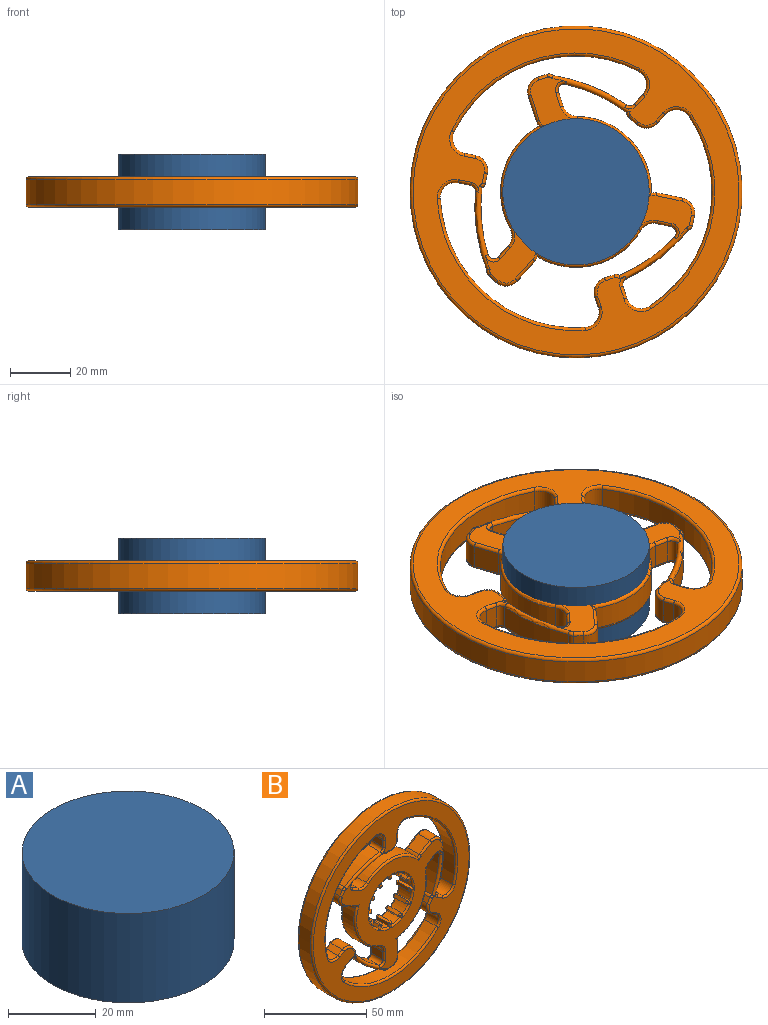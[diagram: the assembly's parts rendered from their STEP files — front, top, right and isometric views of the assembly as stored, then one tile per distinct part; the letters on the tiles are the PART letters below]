
ASSEMBLY  parts=2 mates=1
PART A: 3 faces, bbox 48.5x48.5x25 mm
  f0: cylinder r=24.24mm len=48.48mm, axis (0,0,-1), area 3807.4mm2, adj f1,f2
  f1: plane 48.48x48.48mm, normal (0,0,1), area 1845.8mm2, adj f0
  f2: plane 48.48x48.48mm, normal (0,0,-1), area 1845.8mm2, adj f0
PART B: 301 faces, bbox 119.1x10x119.1 mm
  f0: plane 108x108mm, normal (0,1,0), area 2938.6mm2, adj f185,f188,f189,f192,f193,f196,f197,f199
  f1: plane 108x108mm, normal (0,-1,0), area 2938.6mm2, adj f242,f245,f246,f249,f250,f253,f254,f256
  f2: cylinder r=15mm len=8mm, axis (0,1,0), area 46.8mm2, adj f109,f110,f148,f184
  f3: cylinder r=15mm len=8mm, axis (0,1,0), area 46.8mm2, adj f106,f107,f143,f179
  f4: cylinder r=15mm len=8mm, axis (0,1,0), area 46.8mm2, adj f103,f104,f137,f173
  f5: cylinder r=15mm len=8mm, axis (0,1,0), area 46.8mm2, adj f100,f101,f131,f167
  f6: cylinder r=15mm len=8mm, axis (0,1,0), area 46.8mm2, adj f97,f98,f125,f161
  f7: cylinder r=15mm len=8mm, axis (0,1,0), area 46.8mm2, adj f94,f95,f119,f155
  f8: cylinder r=15mm len=8mm, axis (0,1,0), area 46.8mm2, adj f91,f92,f113,f149
  f9: cylinder r=15mm len=8mm, axis (0,1,0), area 46.8mm2, adj f88,f89,f118,f154
  f10: cylinder r=15mm len=8mm, axis (0,1,0), area 46.8mm2, adj f85,f86,f124,f160
  f11: cylinder r=15mm len=8mm, axis (0,1,0), area 46.8mm2, adj f82,f83,f130,f166
  f12: cylinder r=15mm len=8mm, axis (0,1,0), area 46.8mm2, adj f79,f80,f136,f172
  f13: cylinder r=15mm len=8mm, axis (0,1,0), area 46.8mm2, adj f77,f112,f142,f178
  f14: plane 8x3.59mm, normal (0.5,0,-0.87), area 33.2mm2, adj f58,f65,f189,f249
  f15: plane 8x3.59mm, normal (0.5,0,0.87), area 33.2mm2, adj f61,f67,f210,f269
  f16: plane 8x4.15mm, normal (-1,0,0), area 33.2mm2, adj f64,f69,f230,f288
  f17: cylinder r=45mm len=55.61mm, axis (0,1,0), area 572.1mm2, adj f57,f64,f222,f280
  f18: cylinder r=45mm len=64.22mm, axis (0,1,0), area 572.1mm2, adj f58,f60,f188,f242
  f19: cylinder r=45mm len=55.61mm, axis (0,1,0), area 572.1mm2, adj f61,f63,f217,f277
  f20: cylinder r=55mm len=110mm, axis (0,1,0), area 2764.6mm2, adj f299,f300
  f21: plane 69.83x64.18mm, normal (0,-1,0), area 1385.1mm2, adj f113,f118,f119,f124,f125,f130,f131,f136
  f22: plane 69.83x64.18mm, normal (0,1,0), area 1385.1mm2, adj f149,f154,f155,f160,f161,f166,f167,f172
  f23: plane 8x3.42mm, normal (0,0,-1), area 27.4mm2, adj f62,f76,f233,f293
  f24: plane 8x3.73mm, normal (1,0,0), area 29.8mm2, adj f62,f63,f225,f285
  f25: plane 8x2.96mm, normal (-0.87,0,0.5), area 27.4mm2, adj f59,f75,f201,f257
  f26: plane 8x3.23mm, normal (-0.5,0,-0.87), area 29.8mm2, adj f59,f60,f196,f250
  f27: plane 8x2.96mm, normal (0.87,0,0.5), area 27.4mm2, adj f56,f74,f206,f265
  f28: plane 8x3.23mm, normal (-0.5,0,0.87), area 29.8mm2, adj f56,f57,f214,f272
  f29: cylinder r=55mm len=21.31mm, axis (0,1,0), area 179.4mm2, adj f70,f76,f238,f295
  f30: cylinder r=57mm len=24.52mm, axis (0,1,0), area 210.7mm2, adj f69,f72,f238,f295
  f31: cylinder r=25mm len=29.23mm, axis (0,1,0), area 313mm2, adj f47,f54,f195,f251
  f32: cylinder r=25mm len=35.17mm, axis (0,1,0), area 313mm2, adj f49,f50,f236,f290
  f33: cylinder r=25mm len=31.69mm, axis (0,1,0), area 313mm2, adj f52,f55,f215,f271
  f34: plane 8x4.89mm, normal (-1,0,0), area 39.1mm2, adj f55,f66,f207,f264
  f35: plane 8x3.22mm, normal (0,0,-1), area 25.8mm2, adj f53,f73,f190,f248
  f36: plane 8.73x8mm, normal (1,0,0), area 69.8mm2, adj f53,f54,f187,f243
  f37: plane 8x4.24mm, normal (0.5,0,0.87), area 39.1mm2, adj f50,f70,f240,f297
  f38: plane 8x2.79mm, normal (-0.87,0,0.5), area 25.8mm2, adj f51,f72,f231,f287
  f39: plane 8x7.56mm, normal (-0.5,0,-0.87), area 69.8mm2, adj f51,f52,f223,f279
  f40: plane 8x4.24mm, normal (0.5,0,-0.87), area 39.1mm2, adj f47,f68,f200,f258
  f41: plane 8x2.79mm, normal (0.87,0,0.5), area 25.8mm2, adj f48,f71,f220,f274
  f42: plane 8x7.56mm, normal (-0.5,0,0.87), area 69.8mm2, adj f48,f49,f228,f282
  f43: cylinder r=55mm len=21.7mm, axis (0,1,0), area 179.4mm2, adj f68,f75,f208,f263
  f44: cylinder r=57mm len=25.71mm, axis (0,1,0), area 210.7mm2, adj f67,f71,f208,f263
  f45: cylinder r=55mm len=16.27mm, axis (0,1,0), area 179.4mm2, adj f66,f74,f197,f256
  f46: cylinder r=57mm len=20.01mm, axis (0,1,0), area 210.7mm2, adj f65,f73,f197,f256
  f47: cylinder r=5mm len=8mm, axis (0,1,0), area 49.5mm2, adj f31,f40,f198,f255
  f48: cylinder r=5mm len=8mm, axis (0,-1,0), area 62.8mm2, adj f41,f42,f224,f278
  f49: cylinder r=5mm len=8mm, axis (0,1,0), area 14.3mm2, adj f32,f42,f232,f286
  f50: cylinder r=5mm len=8mm, axis (0,1,0), area 49.5mm2, adj f32,f37,f239,f294
  f51: cylinder r=5mm len=8mm, axis (0,-1,0), area 62.8mm2, adj f38,f39,f227,f283
  f52: cylinder r=5mm len=8mm, axis (0,1,0), area 14.3mm2, adj f33,f39,f219,f275
  f53: cylinder r=5mm len=8mm, axis (0,-1,0), area 62.8mm2, adj f35,f36,f186,f244
  f54: cylinder r=5mm len=8mm, axis (0,1,0), area 14.3mm2, adj f31,f36,f191,f247
  f55: cylinder r=5mm len=8mm, axis (0,1,0), area 49.5mm2, adj f33,f34,f212,f267
  f56: cylinder r=5mm len=8mm, axis (0,-1,0), area 62.8mm2, adj f27,f28,f211,f268
  f57: cylinder r=5mm len=8mm, axis (0,1,0), area 72.9mm2, adj f17,f28,f218,f276
  f58: cylinder r=5mm len=8mm, axis (0,1,0), area 72.9mm2, adj f14,f18,f185,f245
  f59: cylinder r=5mm len=8mm, axis (0,-1,0), area 62.8mm2, adj f25,f26,f199,f254
  f60: cylinder r=5mm len=8mm, axis (0,1,0), area 72.9mm2, adj f18,f26,f192,f246
  f61: cylinder r=5mm len=8mm, axis (0,1,0), area 72.9mm2, adj f15,f19,f213,f273
  f62: cylinder r=5mm len=8mm, axis (0,-1,0), area 62.8mm2, adj f23,f24,f229,f289
  f63: cylinder r=5mm len=8mm, axis (0,1,0), area 72.9mm2, adj f19,f24,f221,f281
  f64: cylinder r=5mm len=8mm, axis (0,1,0), area 72.9mm2, adj f16,f17,f226,f284
  f65: cylinder r=2mm len=8mm, axis (0,1,0), area 23.2mm2, adj f14,f46,f193,f253
  f66: cylinder r=2mm len=8mm, axis (0,1,0), area 33.9mm2, adj f34,f45,f203,f261
  f67: cylinder r=2mm len=8mm, axis (0,1,0), area 23.2mm2, adj f15,f44,f209,f266
  f68: cylinder r=2mm len=8mm, axis (0,1,0), area 33.9mm2, adj f40,f43,f204,f260
  f69: cylinder r=2mm len=8mm, axis (0,1,0), area 23.2mm2, adj f16,f30,f234,f292
  f70: cylinder r=2mm len=8mm, axis (0,1,0), area 33.9mm2, adj f29,f37,f241,f298
  f71: cylinder r=2mm len=8mm, axis (0,1,0), area 17.5mm2, adj f41,f44,f216,f270
  f72: cylinder r=2mm len=8mm, axis (0,1,0), area 17.5mm2, adj f30,f38,f235,f291
  f73: cylinder r=2mm len=8mm, axis (0,1,0), area 17.5mm2, adj f35,f46,f194,f252
  f74: cylinder r=2mm len=8mm, axis (0,1,0), area 14.6mm2, adj f27,f45,f202,f262
  f75: cylinder r=2mm len=8mm, axis (0,1,0), area 14.6mm2, adj f25,f43,f205,f259
  f76: cylinder r=2mm len=8mm, axis (0,1,0), area 14.6mm2, adj f23,f29,f237,f296
  f77: plane 8x1.97mm, normal (-1,0,0), area 15.8mm2, adj f13,f78,f138,f175
  f78: plane 8x2mm, normal (0,0,-1), area 16mm2, adj f77,f79,f139,f174
  f79: plane 8x1.96mm, normal (1,0,0), area 15.7mm2, adj f12,f78,f138,f175
  f80: plane 8x1.71mm, normal (-0.87,0,0.5), area 15.8mm2, adj f12,f81,f132,f169
  f81: plane 8x1.73mm, normal (-0.5,0,-0.87), area 16mm2, adj f80,f82,f133,f168
  f82: plane 8x1.7mm, normal (0.87,0,-0.5), area 15.7mm2, adj f11,f81,f132,f169
  f83: plane 8x1.71mm, normal (-0.5,0,0.87), area 15.8mm2, adj f11,f84,f126,f163
  f84: plane 8x1.73mm, normal (-0.87,0,-0.5), area 16mm2, adj f83,f85,f127,f162
  f85: plane 8x1.7mm, normal (0.5,0,-0.87), area 15.7mm2, adj f10,f84,f126,f163
  f86: plane 8x1.97mm, normal (0,0,1), area 15.8mm2, adj f10,f87,f120,f157
  f87: plane 8x2mm, normal (-1,0,0), area 16mm2, adj f86,f88,f121,f156
  f88: plane 8x1.96mm, normal (0,0,-1), area 15.7mm2, adj f9,f87,f120,f157
  f89: plane 8x1.71mm, normal (0.5,0,0.87), area 15.8mm2, adj f9,f90,f114,f151
  f90: plane 8x1.73mm, normal (-0.87,0,0.5), area 16mm2, adj f89,f91,f115,f150
  f91: plane 8x1.7mm, normal (-0.5,0,-0.87), area 15.7mm2, adj f8,f90,f114,f151
  f92: plane 8x1.71mm, normal (0.87,0,0.5), area 15.8mm2, adj f8,f93,f117,f152
  f93: plane 8x1.73mm, normal (-0.5,0,0.87), area 16mm2, adj f92,f94,f116,f153
  f94: plane 8x1.7mm, normal (-0.87,0,-0.5), area 15.7mm2, adj f7,f93,f117,f152
  f95: plane 8x1.97mm, normal (1,0,0), area 15.8mm2, adj f7,f96,f123,f158
  f96: plane 8x2mm, normal (0,0,1), area 16mm2, adj f95,f97,f122,f159
  f97: plane 8x1.96mm, normal (-1,0,0), area 15.7mm2, adj f6,f96,f123,f158
  f98: plane 8x1.71mm, normal (0.87,0,-0.5), area 15.8mm2, adj f6,f99,f129,f164
  f99: plane 8x1.73mm, normal (0.5,0,0.87), area 16mm2, adj f98,f100,f128,f165
  f100: plane 8x1.7mm, normal (-0.87,0,0.5), area 15.7mm2, adj f5,f99,f129,f164
  f101: plane 8x1.71mm, normal (0.5,0,-0.87), area 15.8mm2, adj f5,f102,f135,f170
  f102: plane 8x1.73mm, normal (0.87,0,0.5), area 16mm2, adj f101,f103,f134,f171
  f103: plane 8x1.7mm, normal (-0.5,0,0.87), area 15.7mm2, adj f4,f102,f135,f170
  f104: plane 8x1.97mm, normal (0,0,-1), area 15.8mm2, adj f4,f105,f141,f176
  f105: plane 8x2mm, normal (1,0,0), area 16mm2, adj f104,f106,f140,f177
  f106: plane 8x1.96mm, normal (0,0,1), area 15.7mm2, adj f3,f105,f141,f176
  f107: plane 8x1.71mm, normal (-0.5,0,-0.87), area 15.8mm2, adj f3,f108,f147,f182
  f108: plane 8x1.73mm, normal (0.87,0,-0.5), area 16mm2, adj f107,f109,f146,f183
  f109: plane 8x1.7mm, normal (0.5,0,0.87), area 15.7mm2, adj f2,f108,f147,f182
  f110: plane 8x1.71mm, normal (-0.87,0,-0.5), area 15.8mm2, adj f2,f111,f144,f181
  f111: plane 8x1.73mm, normal (0.5,0,-0.87), area 16mm2, adj f110,f112,f145,f180
  f112: plane 8x1.7mm, normal (0.87,0,0.5), area 15.7mm2, adj f13,f111,f144,f181
  f113: torus R=16mm, axis (0,-1,0), area 10.6mm2, adj f8,f21,f114,f117
  f114: cylinder r=1mm len=3.6mm, axis (-0.87,0,0.5), area 6.2mm2, adj f89,f91,f113,f115,f118
  f115: cylinder r=1mm len=2.23mm, axis (0.5,0,0.87), area 2mm2, adj f90,f114
  f116: cylinder r=1mm len=2.23mm, axis (0.87,0,0.5), area 2mm2, adj f93,f117
  f117: cylinder r=1mm len=3.6mm, axis (0.5,0,-0.87), area 6.2mm2, adj f92,f94,f113,f116,f119
  f118: torus R=16mm, axis (0,-1,0), area 10.6mm2, adj f9,f21,f114,f120
  f119: torus R=16mm, axis (0,-1,0), area 10.6mm2, adj f7,f21,f117,f123
  f120: cylinder r=1mm len=3mm, axis (-1,0,0), area 6.2mm2, adj f86,f88,f118,f121,f124
  f121: cylinder r=1mm len=2mm, axis (0,0,1), area 2mm2, adj f87,f120
  f122: cylinder r=1mm len=2mm, axis (1,0,0), area 2mm2, adj f96,f123
  f123: cylinder r=1mm len=3mm, axis (0,0,-1), area 6.2mm2, adj f95,f97,f119,f122,f125
  f124: torus R=16mm, axis (0,-1,0), area 10.6mm2, adj f10,f21,f120,f126
  f125: torus R=16mm, axis (0,-1,0), area 10.6mm2, adj f6,f21,f123,f129
  f126: cylinder r=1mm len=3.6mm, axis (-0.87,0,-0.5), area 6.2mm2, adj f83,f85,f124,f127,f130
  f127: cylinder r=1mm len=2.23mm, axis (-0.5,0,0.87), area 2mm2, adj f84,f126
  f128: cylinder r=1mm len=2.23mm, axis (0.87,0,-0.5), area 2mm2, adj f99,f129
  f129: cylinder r=1mm len=3.6mm, axis (-0.5,0,-0.87), area 6.2mm2, adj f98,f100,f125,f128,f131
  f130: torus R=16mm, axis (0,-1,0), area 10.6mm2, adj f11,f21,f126,f132
  f131: torus R=16mm, axis (0,-1,0), area 10.6mm2, adj f5,f21,f129,f135
  f132: cylinder r=1mm len=3.6mm, axis (-0.5,0,-0.87), area 6.2mm2, adj f80,f82,f130,f133,f136
  f133: cylinder r=1mm len=2.23mm, axis (-0.87,0,0.5), area 2mm2, adj f81,f132
  f134: cylinder r=1mm len=2.23mm, axis (0.5,0,-0.87), area 2mm2, adj f102,f135
  f135: cylinder r=1mm len=3.6mm, axis (-0.87,0,-0.5), area 6.2mm2, adj f101,f103,f131,f134,f137
  f136: torus R=16mm, axis (0,-1,0), area 10.6mm2, adj f12,f21,f132,f138
  f137: torus R=16mm, axis (0,-1,0), area 10.6mm2, adj f4,f21,f135,f141
  f138: cylinder r=1mm len=3mm, axis (0,0,-1), area 6.2mm2, adj f77,f79,f136,f139,f142
  f139: cylinder r=1mm len=2mm, axis (-1,0,0), area 2mm2, adj f78,f138
  f140: cylinder r=1mm len=2mm, axis (0,0,-1), area 2mm2, adj f105,f141
  f141: cylinder r=1mm len=3mm, axis (-1,0,0), area 6.2mm2, adj f104,f106,f137,f140,f143
  f142: torus R=16mm, axis (0,-1,0), area 10.6mm2, adj f13,f21,f138,f144
  f143: torus R=16mm, axis (0,-1,0), area 10.6mm2, adj f3,f21,f141,f147
  f144: cylinder r=1mm len=3.6mm, axis (0.5,0,-0.87), area 6.2mm2, adj f110,f112,f142,f145,f148
  f145: cylinder r=1mm len=2.23mm, axis (-0.87,0,-0.5), area 2mm2, adj f111,f144
  f146: cylinder r=1mm len=2.23mm, axis (-0.5,0,-0.87), area 2mm2, adj f108,f147
  f147: cylinder r=1mm len=3.6mm, axis (-0.87,0,0.5), area 6.2mm2, adj f107,f109,f143,f146,f148
  f148: torus R=16mm, axis (0,-1,0), area 10.6mm2, adj f2,f21,f144,f147
  f149: torus R=16mm, axis (0,-1,0), area 10.6mm2, adj f8,f22,f151,f152
  f150: cylinder r=1mm len=2.23mm, axis (-0.5,0,-0.87), area 2mm2, adj f90,f151
  f151: cylinder r=1mm len=3.6mm, axis (0.87,0,-0.5), area 6.2mm2, adj f89,f91,f149,f150,f154
  f152: cylinder r=1mm len=3.6mm, axis (-0.5,0,0.87), area 6.2mm2, adj f92,f94,f149,f153,f155
  f153: cylinder r=1mm len=2.23mm, axis (-0.87,0,-0.5), area 2mm2, adj f93,f152
  f154: torus R=16mm, axis (0,-1,0), area 10.6mm2, adj f9,f22,f151,f157
  f155: torus R=16mm, axis (0,-1,0), area 10.6mm2, adj f7,f22,f152,f158
  f156: cylinder r=1mm len=2mm, axis (0,0,-1), area 2mm2, adj f87,f157
  f157: cylinder r=1mm len=3mm, axis (1,0,0), area 6.2mm2, adj f86,f88,f154,f156,f160
  f158: cylinder r=1mm len=3mm, axis (0,0,1), area 6.2mm2, adj f95,f97,f155,f159,f161
  f159: cylinder r=1mm len=2mm, axis (-1,0,0), area 2mm2, adj f96,f158
  f160: torus R=16mm, axis (0,-1,0), area 10.6mm2, adj f10,f22,f157,f163
  f161: torus R=16mm, axis (0,-1,0), area 10.6mm2, adj f6,f22,f158,f164
  f162: cylinder r=1mm len=2.23mm, axis (0.5,0,-0.87), area 2mm2, adj f84,f163
  f163: cylinder r=1mm len=3.6mm, axis (0.87,0,0.5), area 6.2mm2, adj f83,f85,f160,f162,f166
  f164: cylinder r=1mm len=3.6mm, axis (0.5,0,0.87), area 6.2mm2, adj f98,f100,f161,f165,f167
  f165: cylinder r=1mm len=2.23mm, axis (-0.87,0,0.5), area 2mm2, adj f99,f164
  f166: torus R=16mm, axis (0,-1,0), area 10.6mm2, adj f11,f22,f163,f169
  f167: torus R=16mm, axis (0,-1,0), area 10.6mm2, adj f5,f22,f164,f170
  f168: cylinder r=1mm len=2.23mm, axis (0.87,0,-0.5), area 2mm2, adj f81,f169
  f169: cylinder r=1mm len=3.6mm, axis (0.5,0,0.87), area 6.2mm2, adj f80,f82,f166,f168,f172
  f170: cylinder r=1mm len=3.6mm, axis (0.87,0,0.5), area 6.2mm2, adj f101,f103,f167,f171,f173
  f171: cylinder r=1mm len=2.23mm, axis (-0.5,0,0.87), area 2mm2, adj f102,f170
  f172: torus R=16mm, axis (0,-1,0), area 10.6mm2, adj f12,f22,f169,f175
  f173: torus R=16mm, axis (0,-1,0), area 10.6mm2, adj f4,f22,f170,f176
  f174: cylinder r=1mm len=2mm, axis (1,0,0), area 2mm2, adj f78,f175
  f175: cylinder r=1mm len=3mm, axis (0,0,1), area 6.2mm2, adj f77,f79,f172,f174,f178
  f176: cylinder r=1mm len=3mm, axis (1,0,0), area 6.2mm2, adj f104,f106,f173,f177,f179
  f177: cylinder r=1mm len=2mm, axis (0,0,1), area 2mm2, adj f105,f176
  f178: torus R=16mm, axis (0,-1,0), area 10.6mm2, adj f13,f22,f175,f181
  f179: torus R=16mm, axis (0,-1,0), area 10.6mm2, adj f3,f22,f176,f182
  f180: cylinder r=1mm len=2.23mm, axis (0.87,0,0.5), area 2mm2, adj f111,f181
  f181: cylinder r=1mm len=3.6mm, axis (-0.5,0,0.87), area 6.2mm2, adj f110,f112,f178,f180,f184
  f182: cylinder r=1mm len=3.6mm, axis (0.87,0,-0.5), area 6.2mm2, adj f107,f109,f179,f183,f184
  f183: cylinder r=1mm len=2.23mm, axis (0.5,0,0.87), area 2mm2, adj f108,f182
  f184: torus R=16mm, axis (0,-1,0), area 10.6mm2, adj f2,f22,f181,f182
  f185: torus R=6mm, axis (0,-1,0), area 15.4mm2, adj f0,f58,f188,f189
  f186: torus R=4mm, axis (0,-1,0), area 11.4mm2, adj f22,f53,f187,f190
  f187: cylinder r=1mm len=8.73mm, axis (0,0,1), area 13.7mm2, adj f22,f36,f186,f191
  f188: torus R=46mm, axis (0,-1,0), area 113.2mm2, adj f0,f18,f185,f192
  f189: cylinder r=1mm len=4.09mm, axis (0.87,0,0.5), area 6.5mm2, adj f0,f14,f185,f193
  f190: cylinder r=1mm len=3.22mm, axis (1,0,0), area 5.1mm2, adj f22,f35,f186,f194
  f191: torus R=4mm, axis (0,-1,0), area 3.3mm2, adj f22,f54,f187,f195
  f192: torus R=6mm, axis (0,-1,0), area 15.4mm2, adj f0,f60,f188,f196
  f193: torus R=3mm, axis (0,-1,0), area 5.4mm2, adj f0,f65,f189,f197
  f194: torus R=1mm, axis (0,-1,0), area 3mm2, adj f22,f73,f190,f197
  f195: torus R=24mm, axis (0,-1,0), area 61.3mm2, adj f22,f31,f191,f198
  f196: cylinder r=1mm len=3.73mm, axis (0.87,0,-0.5), area 5.9mm2, adj f0,f26,f192,f199
  f197: torus R=56mm, axis (0,-1,0), area 77.1mm2, adj f0,f22,f45,f46,f193,f194,f202,f203
  f198: torus R=6mm, axis (0,-1,0), area 10.4mm2, adj f22,f47,f195,f200
  f199: torus R=4mm, axis (0,-1,0), area 11.4mm2, adj f0,f59,f196,f201
  f200: cylinder r=1mm len=4.74mm, axis (0.87,0,0.5), area 7.7mm2, adj f22,f40,f198,f204
  f201: cylinder r=1mm len=3.46mm, axis (-0.5,0,-0.87), area 5.4mm2, adj f0,f25,f199,f205
  f202: torus R=1mm, axis (0,-1,0), area 2.6mm2, adj f0,f74,f197,f206
  f203: torus R=3mm, axis (0,-1,0), area 7.9mm2, adj f22,f66,f197,f207
  f204: torus R=3mm, axis (0,-1,0), area 7.9mm2, adj f22,f68,f200,f208
  f205: torus R=1mm, axis (0,-1,0), area 2.6mm2, adj f0,f75,f201,f208
  f206: cylinder r=1mm len=3.46mm, axis (-0.5,0,0.87), area 5.4mm2, adj f0,f27,f202,f211
  f207: cylinder r=1mm len=4.89mm, axis (0,0,-1), area 7.7mm2, adj f22,f34,f203,f212
  f208: torus R=56mm, axis (0,-1,0), area 77.1mm2, adj f0,f22,f43,f44,f204,f205,f209,f216
  f209: torus R=3mm, axis (0,-1,0), area 5.4mm2, adj f0,f67,f208,f210
  f210: cylinder r=1mm len=4.09mm, axis (-0.87,0,0.5), area 6.5mm2, adj f0,f15,f209,f213
  f211: torus R=4mm, axis (0,-1,0), area 11.4mm2, adj f0,f56,f206,f214
  f212: torus R=6mm, axis (0,-1,0), area 10.4mm2, adj f22,f55,f207,f215
  f213: torus R=6mm, axis (0,-1,0), area 15.4mm2, adj f0,f61,f210,f217
  f214: cylinder r=1mm len=3.73mm, axis (-0.87,0,-0.5), area 5.9mm2, adj f0,f28,f211,f218
  f215: torus R=24mm, axis (0,-1,0), area 61.3mm2, adj f22,f33,f212,f219
  f216: torus R=1mm, axis (0,-1,0), area 3mm2, adj f22,f71,f208,f220
  f217: torus R=46mm, axis (0,-1,0), area 113.2mm2, adj f0,f19,f213,f221
  f218: torus R=6mm, axis (0,-1,0), area 15.4mm2, adj f0,f57,f214,f222
  f219: torus R=4mm, axis (0,-1,0), area 3.3mm2, adj f22,f52,f215,f223
  f220: cylinder r=1mm len=3.29mm, axis (-0.5,0,0.87), area 5.1mm2, adj f22,f41,f216,f224
  f221: torus R=6mm, axis (0,-1,0), area 15.4mm2, adj f0,f63,f217,f225
  f222: torus R=46mm, axis (0,-1,0), area 113.2mm2, adj f0,f17,f218,f226
  f223: cylinder r=1mm len=8.06mm, axis (0.87,0,-0.5), area 13.7mm2, adj f22,f39,f219,f227
  f224: torus R=4mm, axis (0,-1,0), area 11.4mm2, adj f22,f48,f220,f228
  f225: cylinder r=1mm len=3.73mm, axis (0,0,1), area 5.9mm2, adj f0,f24,f221,f229
  f226: torus R=6mm, axis (0,-1,0), area 15.4mm2, adj f0,f64,f222,f230
  f227: torus R=4mm, axis (0,-1,0), area 11.4mm2, adj f22,f51,f223,f231
  f228: cylinder r=1mm len=8.06mm, axis (-0.87,0,-0.5), area 13.7mm2, adj f22,f42,f224,f232
  f229: torus R=4mm, axis (0,-1,0), area 11.4mm2, adj f0,f62,f225,f233
  f230: cylinder r=1mm len=4.15mm, axis (0,0,-1), area 6.5mm2, adj f0,f16,f226,f234
  f231: cylinder r=1mm len=3.29mm, axis (-0.5,0,-0.87), area 5.1mm2, adj f22,f38,f227,f235
  f232: torus R=4mm, axis (0,-1,0), area 3.3mm2, adj f22,f49,f228,f236
  f233: cylinder r=1mm len=3.42mm, axis (1,0,0), area 5.4mm2, adj f0,f23,f229,f237
  f234: torus R=3mm, axis (0,-1,0), area 5.4mm2, adj f0,f69,f230,f238
  f235: torus R=1mm, axis (0,-1,0), area 3mm2, adj f22,f72,f231,f238
  f236: torus R=24mm, axis (0,-1,0), area 61.3mm2, adj f22,f32,f232,f239
  f237: torus R=1mm, axis (0,-1,0), area 2.6mm2, adj f0,f76,f233,f238
  f238: torus R=56mm, axis (0,-1,0), area 77.1mm2, adj f0,f22,f29,f30,f234,f235,f237,f241
  f239: torus R=6mm, axis (0,-1,0), area 10.4mm2, adj f22,f50,f236,f240
  f240: cylinder r=1mm len=4.74mm, axis (-0.87,0,0.5), area 7.7mm2, adj f22,f37,f239,f241
  f241: torus R=3mm, axis (0,-1,0), area 7.9mm2, adj f22,f70,f238,f240
  f242: torus R=46mm, axis (0,-1,0), area 113.2mm2, adj f1,f18,f245,f246
  f243: cylinder r=1mm len=8.73mm, axis (0,0,-1), area 13.7mm2, adj f21,f36,f244,f247
  f244: torus R=4mm, axis (0,-1,0), area 11.4mm2, adj f21,f53,f243,f248
  f245: torus R=6mm, axis (0,-1,0), area 15.4mm2, adj f1,f58,f242,f249
  f246: torus R=6mm, axis (0,-1,0), area 15.4mm2, adj f1,f60,f242,f250
  f247: torus R=4mm, axis (0,-1,0), area 3.3mm2, adj f21,f54,f243,f251
  f248: cylinder r=1mm len=3.22mm, axis (-1,0,0), area 5.1mm2, adj f21,f35,f244,f252
  f249: cylinder r=1mm len=4.09mm, axis (-0.87,0,-0.5), area 6.5mm2, adj f1,f14,f245,f253
  f250: cylinder r=1mm len=3.73mm, axis (-0.87,0,0.5), area 5.9mm2, adj f1,f26,f246,f254
  f251: torus R=24mm, axis (0,-1,0), area 61.3mm2, adj f21,f31,f247,f255
  f252: torus R=1mm, axis (0,-1,0), area 3mm2, adj f21,f73,f248,f256
  f253: torus R=3mm, axis (0,-1,0), area 5.4mm2, adj f1,f65,f249,f256
  f254: torus R=4mm, axis (0,-1,0), area 11.4mm2, adj f1,f59,f250,f257
  f255: torus R=6mm, axis (0,-1,0), area 10.4mm2, adj f21,f47,f251,f258
  f256: torus R=56mm, axis (0,-1,0), area 77.1mm2, adj f1,f21,f45,f46,f252,f253,f261,f262
  f257: cylinder r=1mm len=3.46mm, axis (0.5,0,0.87), area 5.4mm2, adj f1,f25,f254,f259
  f258: cylinder r=1mm len=4.74mm, axis (-0.87,0,-0.5), area 7.7mm2, adj f21,f40,f255,f260
  f259: torus R=1mm, axis (0,-1,0), area 2.6mm2, adj f1,f75,f257,f263
  f260: torus R=3mm, axis (0,-1,0), area 7.9mm2, adj f21,f68,f258,f263
  f261: torus R=3mm, axis (0,-1,0), area 7.9mm2, adj f21,f66,f256,f264
  f262: torus R=1mm, axis (0,-1,0), area 2.6mm2, adj f1,f74,f256,f265
  f263: torus R=56mm, axis (0,-1,0), area 77.1mm2, adj f1,f21,f43,f44,f259,f260,f266,f270
  f264: cylinder r=1mm len=4.89mm, axis (0,0,1), area 7.7mm2, adj f21,f34,f261,f267
  f265: cylinder r=1mm len=3.46mm, axis (0.5,0,-0.87), area 5.4mm2, adj f1,f27,f262,f268
  f266: torus R=3mm, axis (0,-1,0), area 5.4mm2, adj f1,f67,f263,f269
  f267: torus R=6mm, axis (0,-1,0), area 10.4mm2, adj f21,f55,f264,f271
  f268: torus R=4mm, axis (0,-1,0), area 11.4mm2, adj f1,f56,f265,f272
  f269: cylinder r=1mm len=4.09mm, axis (0.87,0,-0.5), area 6.5mm2, adj f1,f15,f266,f273
  f270: torus R=1mm, axis (0,-1,0), area 3mm2, adj f21,f71,f263,f274
  f271: torus R=24mm, axis (0,-1,0), area 61.3mm2, adj f21,f33,f267,f275
  f272: cylinder r=1mm len=3.73mm, axis (0.87,0,0.5), area 5.9mm2, adj f1,f28,f268,f276
  f273: torus R=6mm, axis (0,-1,0), area 15.4mm2, adj f1,f61,f269,f277
  f274: cylinder r=1mm len=3.29mm, axis (0.5,0,-0.87), area 5.1mm2, adj f21,f41,f270,f278
  f275: torus R=4mm, axis (0,-1,0), area 3.3mm2, adj f21,f52,f271,f279
  f276: torus R=6mm, axis (0,-1,0), area 15.4mm2, adj f1,f57,f272,f280
  f277: torus R=46mm, axis (0,-1,0), area 113.2mm2, adj f1,f19,f273,f281
  f278: torus R=4mm, axis (0,-1,0), area 11.4mm2, adj f21,f48,f274,f282
  f279: cylinder r=1mm len=8.06mm, axis (-0.87,0,0.5), area 13.7mm2, adj f21,f39,f275,f283
  f280: torus R=46mm, axis (0,-1,0), area 113.2mm2, adj f1,f17,f276,f284
  f281: torus R=6mm, axis (0,-1,0), area 15.4mm2, adj f1,f63,f277,f285
  f282: cylinder r=1mm len=8.06mm, axis (0.87,0,0.5), area 13.7mm2, adj f21,f42,f278,f286
  f283: torus R=4mm, axis (0,-1,0), area 11.4mm2, adj f21,f51,f279,f287
  f284: torus R=6mm, axis (0,-1,0), area 15.4mm2, adj f1,f64,f280,f288
  f285: cylinder r=1mm len=3.73mm, axis (0,0,-1), area 5.9mm2, adj f1,f24,f281,f289
  f286: torus R=4mm, axis (0,-1,0), area 3.3mm2, adj f21,f49,f282,f290
  f287: cylinder r=1mm len=3.29mm, axis (0.5,0,0.87), area 5.1mm2, adj f21,f38,f283,f291
  f288: cylinder r=1mm len=4.15mm, axis (0,0,1), area 6.5mm2, adj f1,f16,f284,f292
  f289: torus R=4mm, axis (0,-1,0), area 11.4mm2, adj f1,f62,f285,f293
  f290: torus R=24mm, axis (0,-1,0), area 61.3mm2, adj f21,f32,f286,f294
  f291: torus R=1mm, axis (0,-1,0), area 3mm2, adj f21,f72,f287,f295
  f292: torus R=3mm, axis (0,-1,0), area 5.4mm2, adj f1,f69,f288,f295
  f293: cylinder r=1mm len=3.42mm, axis (-1,0,0), area 5.4mm2, adj f1,f23,f289,f296
  f294: torus R=6mm, axis (0,-1,0), area 10.4mm2, adj f21,f50,f290,f297
  f295: torus R=56mm, axis (0,-1,0), area 77.1mm2, adj f1,f21,f29,f30,f291,f292,f296,f298
  f296: torus R=1mm, axis (0,-1,0), area 2.6mm2, adj f1,f76,f293,f295
  f297: cylinder r=1mm len=4.74mm, axis (0.87,0,-0.5), area 7.7mm2, adj f21,f37,f294,f298
  f298: torus R=3mm, axis (0,-1,0), area 7.9mm2, adj f21,f70,f295,f297
  f299: torus R=54mm, axis (0,-1,0), area 539.2mm2, adj f0,f20
  f300: torus R=54mm, axis (0,-1,0), area 539.2mm2, adj f1,f20
PLACE A at identity fixed
PLACE B rot(axis=(-0.88,0.34,-0.34),97.3deg) t=(0,0,7.5)mm
MATE revolute B.f17 <-> A.f0  axis (0,0,-1) through (0,0,12.5)mm
